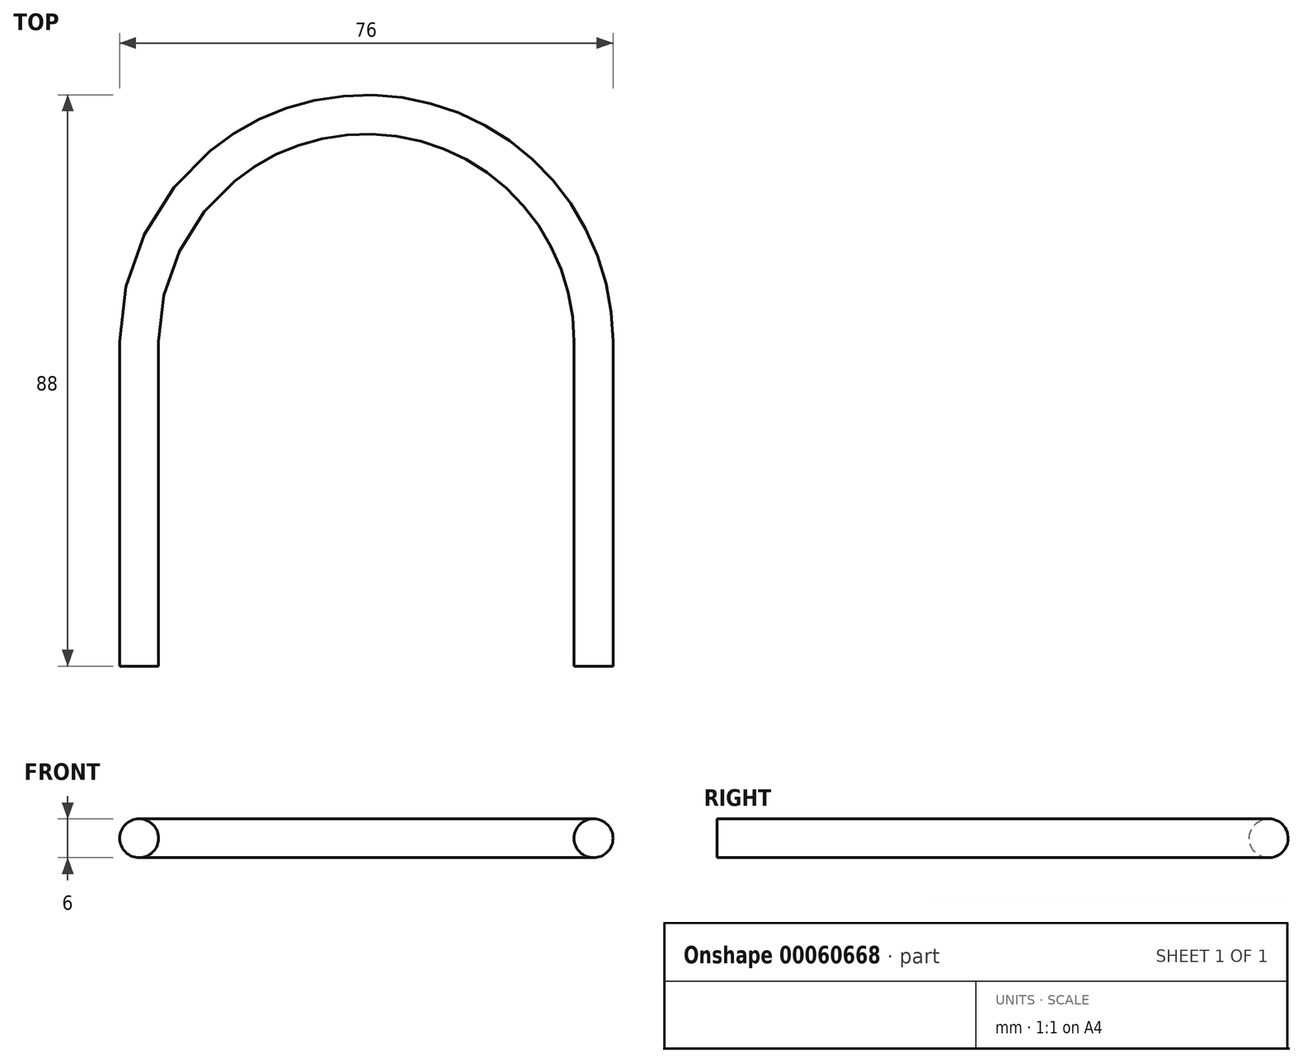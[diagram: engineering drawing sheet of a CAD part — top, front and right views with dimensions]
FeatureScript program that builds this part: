
annotation { "Feature Type Name" : "Feature", "Feature Type Description" : "" }
export const myFeature = defineFeature(function(context is Context, id is Id, definition is map)
    precondition{}
    {
        {
            var Q0;
            Q0=qCreatedBy(makeId("Front.planeOp"),FACE);
            var sketch = newSketch(context, id + "F0", { "sketchPlane" : qUnion([Q0])});
            skCircle(sketch, "E0", {"center": v(0, 0) * mm, "radius": 3 * mm});
            skSolve(sketch);
        }
        {
            var Q0;
            Q0=qCreatedBy(makeId("Top.planeOp"),FACE);
            var sketch = newSketch(context, id + "F1", { "sketchPlane" : qUnion([Q0])});
            skLineSegment(sketch, "E1", {"start": v(0, 0) * mm, "end": v(0, 50) * mm});
            skLineSegment(sketch, "E2", {"start": v(70, 50) * mm, "end": v(70, 0) * mm});
            skArc(sketch, "E3", {"start": v(70, 50) * mm, "mid": v(35, 85) * mm, "end": v(0, 50) * mm});
            skSolve(sketch);
        }
        {
            var Q0;
            Q0 = qSketchRegion(id + "F0", true);
            var Q1;
            Q1=sQuery(id+"F1.wireOp",EDGE,"E1");
            var Q2;
            Q2=sQuery(id+"F1.wireOp",EDGE,"E3");
            var Q3;
            Q3=sQuery(id+"F1.wireOp",EDGE,"E2");
            sweep(context, id + "F2", {"profiles" : qUnion([Q0]), "path" : qUnion([Q1, Q2, Q3])});
        }
    });
